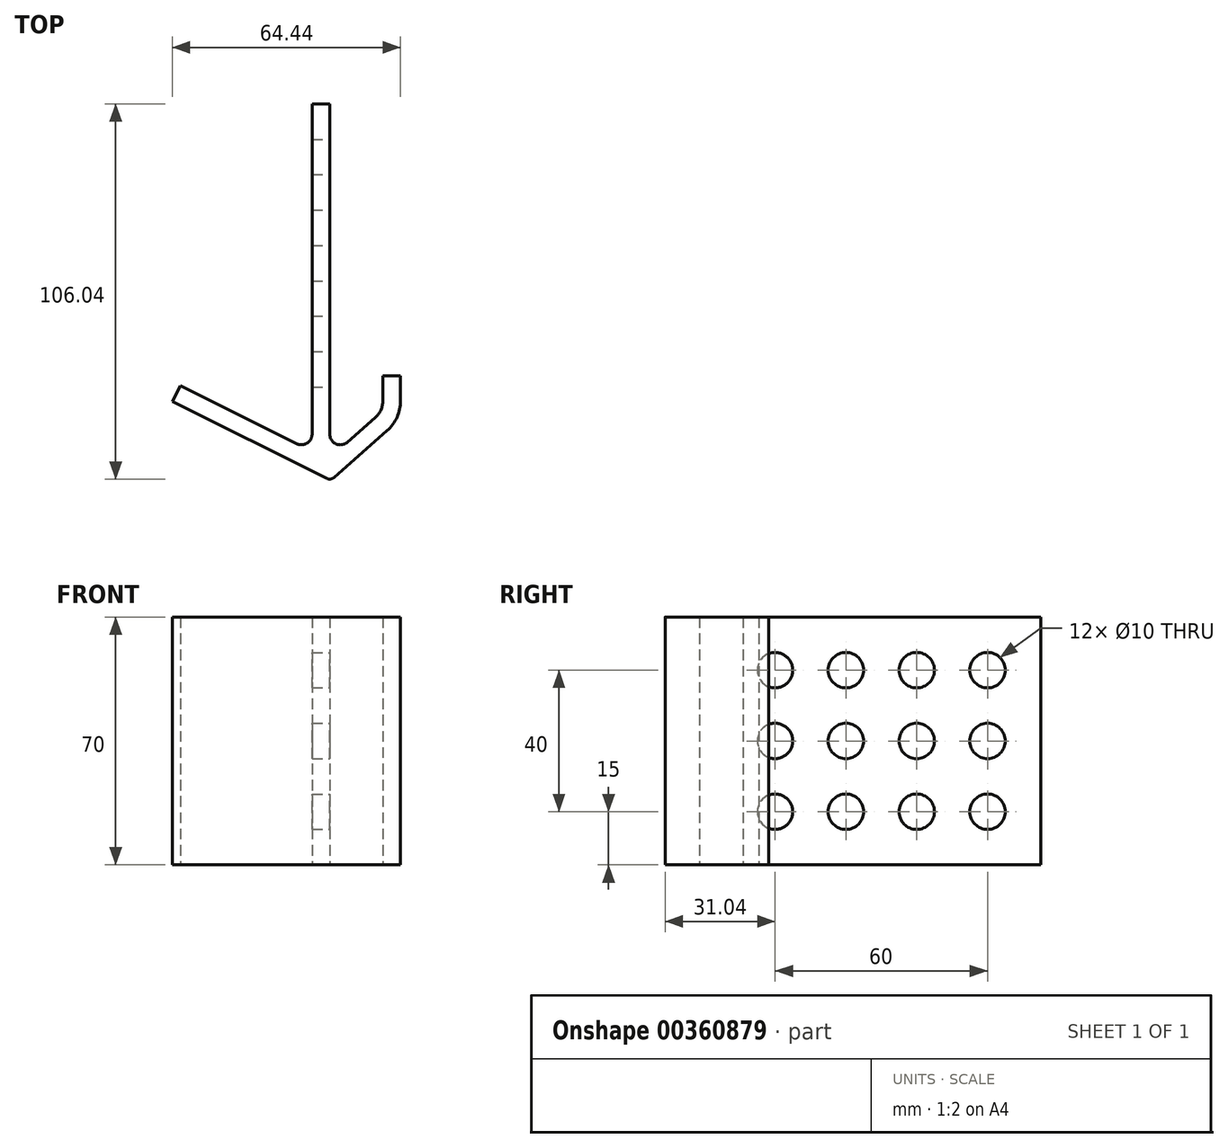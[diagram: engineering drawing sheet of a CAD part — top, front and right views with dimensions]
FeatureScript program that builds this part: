
annotation { "Feature Type Name" : "Feature", "Feature Type Description" : "" }
export const myFeature = defineFeature(function(context is Context, id is Id, definition is map)
    precondition{}
    {
        {
            var Q0;
            Q0=qCreatedBy(makeId("Top.planeOp"),FACE);
            var sketch = newSketch(context, id + "F0", { "sketchPlane" : qUnion([Q0])});
            skLineSegment(sketch, "E0", {"start": v(-17.66, 61.4) * mm, "end": v(-17.66, -31.93) * mm});
            skLineSegment(sketch, "E1", {"start": v(-27, -34.62) * mm, "end": v(-59.86, -18.18) * mm});
            skLineSegment(sketch, "E2", {"start": v(-12.67, -34.18) * mm, "end": v(-4.8, -27.22) * mm});
            skLineSegment(sketch, "E3", {"start": v(-2.66, -22.47) * mm, "end": v(-2.66, -15.4) * mm});
            skPoint(sketch, "E4.visualSharp", {"position": v(-2.66, -25.33) * mm});
            skArc(sketch, "E4.filletArc", {"start": v(-4.8, -27.22) * mm, "mid": v(-3.22, -25.08) * mm, "end": v(-2.66, -22.47) * mm});
            skLineSegment(sketch, "E5.0", {"start": v(-22.66, 61.4) * mm, "end": v(-22.66, -31.93) * mm});
            skLineSegment(sketch, "E6.0", {"start": v(-17.38, -45.02) * mm, "end": v(-62.1, -22.66) * mm});
            skLineSegment(sketch, "E6.1", {"start": v(-17.38, -45.02) * mm, "end": v(-1.49, -30.97) * mm});
            skArc(sketch, "E6.2", {"start": v(-1.49, -30.97) * mm, "mid": v(1.34, -27.13) * mm, "end": v(2.34, -22.47) * mm});
            skLineSegment(sketch, "E6.3", {"start": v(2.34, -22.47) * mm, "end": v(2.34, -15.4) * mm});
            skLineSegment(sketch, "E7", {"start": v(-22.66, 61.4) * mm, "end": v(-17.66, 61.4) * mm});
            skLineSegment(sketch, "E8", {"start": v(-59.86, -18.18) * mm, "end": v(-62.1, -22.66) * mm});
            skLineSegment(sketch, "E9", {"start": v(2.34, -15.4) * mm, "end": v(-2.66, -15.4) * mm});
            skPoint(sketch, "E10.visualSharp", {"position": v(-17.66, -38.6) * mm});
            skArc(sketch, "E10.filletArc", {"start": v(-17.66, -31.93) * mm, "mid": v(-15.89, -34.67) * mm, "end": v(-12.67, -34.18) * mm});
            skArc(sketch, "E11.filletArc", {"start": v(-27, -34.62) * mm, "mid": v(-24.08, -34.49) * mm, "end": v(-22.66, -31.93) * mm});
            skSolve(sketch);
        }
        {
            var Q0;
            Q0 = qSketchRegion(id + "F0", true);
            extrude(context, id + "F1", {"entities" : qUnion([Q0]), "depth" : 70 * mm});
        }
        {
            var Q0;
            Q0=makeQuery(id+"F1.opExtrude","SWEPT_FACE",FACE,{"disambiguationData":[OSD([sQuery(id+"F0.wireOp",EDGE,"E0")])]});
            var sketch = newSketch(context, id + "F2", { "sketchPlane" : qUnion([Q0])});
            skCircle(sketch, "E12", {"center": v(46.4, 55) * mm, "radius": 5 * mm});
            skCircle(sketch, "E13.0.1.0", {"center": v(46.4, 35) * mm, "radius": 5 * mm});
            skCircle(sketch, "E13.0.2.0", {"center": v(46.4, 15) * mm, "radius": 5 * mm});
            skCircle(sketch, "E13.1.0.0", {"center": v(26.4, 55) * mm, "radius": 5 * mm});
            skCircle(sketch, "E13.1.1.0", {"center": v(26.4, 35) * mm, "radius": 5 * mm});
            skCircle(sketch, "E13.1.2.0", {"center": v(26.4, 15) * mm, "radius": 5 * mm});
            skCircle(sketch, "E13.2.0.0", {"center": v(6.4, 55) * mm, "radius": 5 * mm});
            skCircle(sketch, "E13.2.1.0", {"center": v(6.4, 35) * mm, "radius": 5 * mm});
            skCircle(sketch, "E13.2.2.0", {"center": v(6.4, 15) * mm, "radius": 5 * mm});
            skCircle(sketch, "E13.3.0.0", {"center": v(-13.6, 55) * mm, "radius": 5 * mm});
            skCircle(sketch, "E13.3.1.0", {"center": v(-13.6, 35) * mm, "radius": 5 * mm});
            skCircle(sketch, "E13.3.2.0", {"center": v(-13.6, 15) * mm, "radius": 5 * mm});
            skLineSegment(sketch, "E13.direction1", {"start": v(46.4, 55) * mm, "end": v(26.4, 55) * mm, "construction": true});
            skLineSegment(sketch, "E13.direction2", {"start": v(46.4, 55) * mm, "end": v(46.4, 35) * mm, "construction": true});
            skSolve(sketch);
        }
        {
            var Q0;
            Q0 = qSketchRegion(id + "F2", true);
            extrude(context, id + "F3", {"entities" : qUnion([Q0]), "operationType" : NewBodyOperationType.REMOVE, "oppositeDirection" : true, "depth" : 25 * mm});
        }
        {
            var Q0;
            Q0=makeQuery(id+"F1.opExtrude","SWEPT_EDGE",EDGE,{"disambiguationData":[OSD([sQuery(id+"F0.wireOp",EDGE,"E6.0"),sQuery(id+"F0.wireOp",EDGE,"E6.1")])]});
            fillet(context, id + "F4", {"entities" : qUnion([Q0]), "radius" : 2 * mm, "tangentPropagation" : true, "allowEdgeOverflow" : false});
        }
    });
